# Revit family: QF_ELECTROLUXPROFESSIONAL_589722_MCJBEAEOAA
name_source: partatom
category: Attrezzature speciali
units: mm (PartAtom-declared; Revit-internal decimal feet)

## family parameters
Attiva taglio nelle viste = No
Basato su piano di lavoro = No
Condiviso = No
Mantieni orientamento annotazione = No
Punto di calcolo locali = No
Quota connettore circolare = Usa diametro
Sempre verticale = Sì
Taglio con vuoti quando caricato = No
Tipo di parte = Normale

## types (1)
- QF_ELECTROLUXPROFESSIONAL_589722_MCJBEAEOAA
    Conn Conduit = Sì
    Descrizione = FULL IND,CUPB,H2,4ZONE,2S,1000X900X800H
    Direct Waste Size = 0"
    Electrical Remarks = 400 V/3N ph/50/60 Hz
    HP = 37.5 HP
    Max Overcurrent Protection = 0 A
    Min Ckt Ampacity = 0 A
    Modello = 589371
    Phase = 3
    Produttore = ELECTROLUX
    Prospetto di default = 0 mm  [stored 0 ft]
    Volts = 400 V
    Watts = 28000 W
    Weight in Pounds = 299.8

note: [stored X ft] marks values corroborated as IEEE doubles in the binary element streams (Revit-internal decimal feet)

## geometry (parser evidence)
native form markers: Sweep x2
no freeform markers — native parametric forms only
